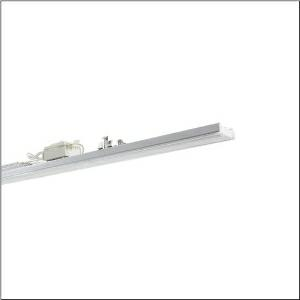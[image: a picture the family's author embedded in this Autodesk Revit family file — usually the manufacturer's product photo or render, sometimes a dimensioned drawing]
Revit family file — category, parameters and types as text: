
# Revit family: licross_11_recessed_mo_51tl11de45xg
name_source: partatom
category: Lighting Fixtures
units: mm (PartAtom-declared; Revit-internal decimal feet)

## family parameters
Cut with Voids When Loaded = No
Host = Face
Light Source = No
Part Type = Normal
Room Calculation Point = No
Round Connector Dimension = Use Diameter
Shared = No

## types (1)
- --- (1 x LED, 5040 lm, 29.6 W, 4000K)
    Apparent Load = 30 VA
    CIE Flux Codes = 89 96 99 100 100
    Color Rendering = 80
    Color Temperature = 4000K
    Default Elevation = 1800 mm
    Description = Licross 11 Recessed MO, luminaire insert, of sheet steel, coil coated, white, length: 750mm, width: 66mm, height: 67mm, LED rated luminous flux: 5.040lm, light colour: 840, SDCM (Standard Deviation of Colour Matching)MacAdam ≤ 2 SDCM (initial), control gear: DALI 2, with plug, 5-pole, with phase selection, mains connection: 220..240V, AC, 50/60Hz, rated input power: 30W, internal wiring halogen-free, primary light control with lens, of plastic, primary optical cover: cover, of PMMA, light emission: direct distribution, primary light characteristic: symmetric, protection rating (complete): IP40, insulation class (complete): insulation class I (protective earthing), certification: CE, ENEC, VDE, UKCA, protection symbol: D if used in an environment without relevant dust loads with corresponding accessories, impact resistance: IK06, permissible ambient temperature for indoor applications: -25..+35°C, corresponds to IFS (International Featured Standards) requirements for safety and quality in the food industry, reducing of maximum allowable ambient temperature of 5°C with ceiling mounting, LABS conformity tested according to VDMA 24364:2018-05, The light source and the operating device comply with the requirements of the Ecodesign Regulation (EU) 2019/2020 and are replaceable in accordance with this regulation, packaging unit: 1 piece
    Height = 58 mm
    Lamp = 1 x LED
    Lamp Light Flux = 5040 lm
    Lamp Power = 29.6 W
    Lamp count = 1
    Length = 750 mm
    Luminous efficacy = 170 lm/W
    Manufacturer = Siteco
    ModVariant = No
    Model = 51TL11DE45XG
    Mounting Place = Ceiling
    Mounting Type = Pendant
    Number of Poles = 1
    OnlyDefault = Yes
    Power Factor = 1
    Product Name = Licross 11 Recessed MO
    Product group = luminaire insert | ceiling pendant
    ProductGroupID = 901
    Protection Class = Protection class I
    Protection Degree = IP 40
    RLX_Detail_Level = 1
    RLX_Emergency_Light_Flux = 0 lm
    RLX_Emergency_Type = 0
    RLX_Emergency_Type_DB = No
    RlxData = <blob elided: 29481 chars, md5=67b8a947>
    Socket = socket
    Standby Power = 0 W
    System Light Flux = 5040 lm
    System Power = 30 W
    Type Comments = factory setting: luminous flux: 100 % | dim-lin: 254 | 378 mA
    Type Image = l_1296930.jpg
    URL = http://relux.com
    VarID = @adj_100113
    Voltage = 0 V
    Weight = 0.00 kg
    Width = 66 mm

## geometry (parser evidence)
native form markers: Blend x4, Sweep x9
no freeform markers — native parametric forms only
